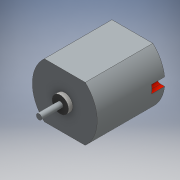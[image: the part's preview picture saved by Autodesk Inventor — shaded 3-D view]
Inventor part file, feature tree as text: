
AUTODESK INVENTOR PART (.ipt)
format: ipt  version: 2016 (Build 200138000, 138)  size: 191,488 bytes
history: native  units: mm
features: extrude x7, sketch x7, other x1, mirror x1
ambient origin geometry x8: Origin, YZ Plane, XZ Plane, XY Plane, X Axis, Y Axis, Z Axis, Center Point
bodies: Body1 (feature_tree)
feature tree (16):
  other  "Sólido1"
  extrude  "Extrusión1"  Depth=4.8mm TaperAngle=0.0deg
  extrude  "Extrusión2"  Depth=2.4mm TaperAngle=0.0deg
  mirror  "Simetría1"
  extrude  "Extrusión3"  Depth=1.6mm TaperAngle=0.0deg
  extrude  "Extrusión4"  [1 undecoded]
  extrude  "Extrusión5"  [1 undecoded]
  extrude  "Extrusión6"  [1 undecoded]
  extrude  "Extrusión7"  [1 undecoded]
  sketch  "Boceto1"  dims[d7=20.0mm d8=0.0mm d23=4.8mm d24=0.0mm]
  sketch  "Boceto3"  dims[d29=1.6mm d30=0.0mm d37=2.4mm d38=0.0mm]
  sketch  "Boceto6"  dims[d39=3.1mm d40=0.0mm d43=1.6mm d44=0.0mm]
  sketch  "Boceto7"  dims[d45=9.4mm d46=0.0mm]
  sketch  "Boceto8"
  sketch  "Boceto9"
  sketch  "Boceto10"
note: 4 required parameter values undecoded (feature->parameter linkage not recoverable at this tier; creation-order binding heuristic only, values carry confidence <= 0.55)
